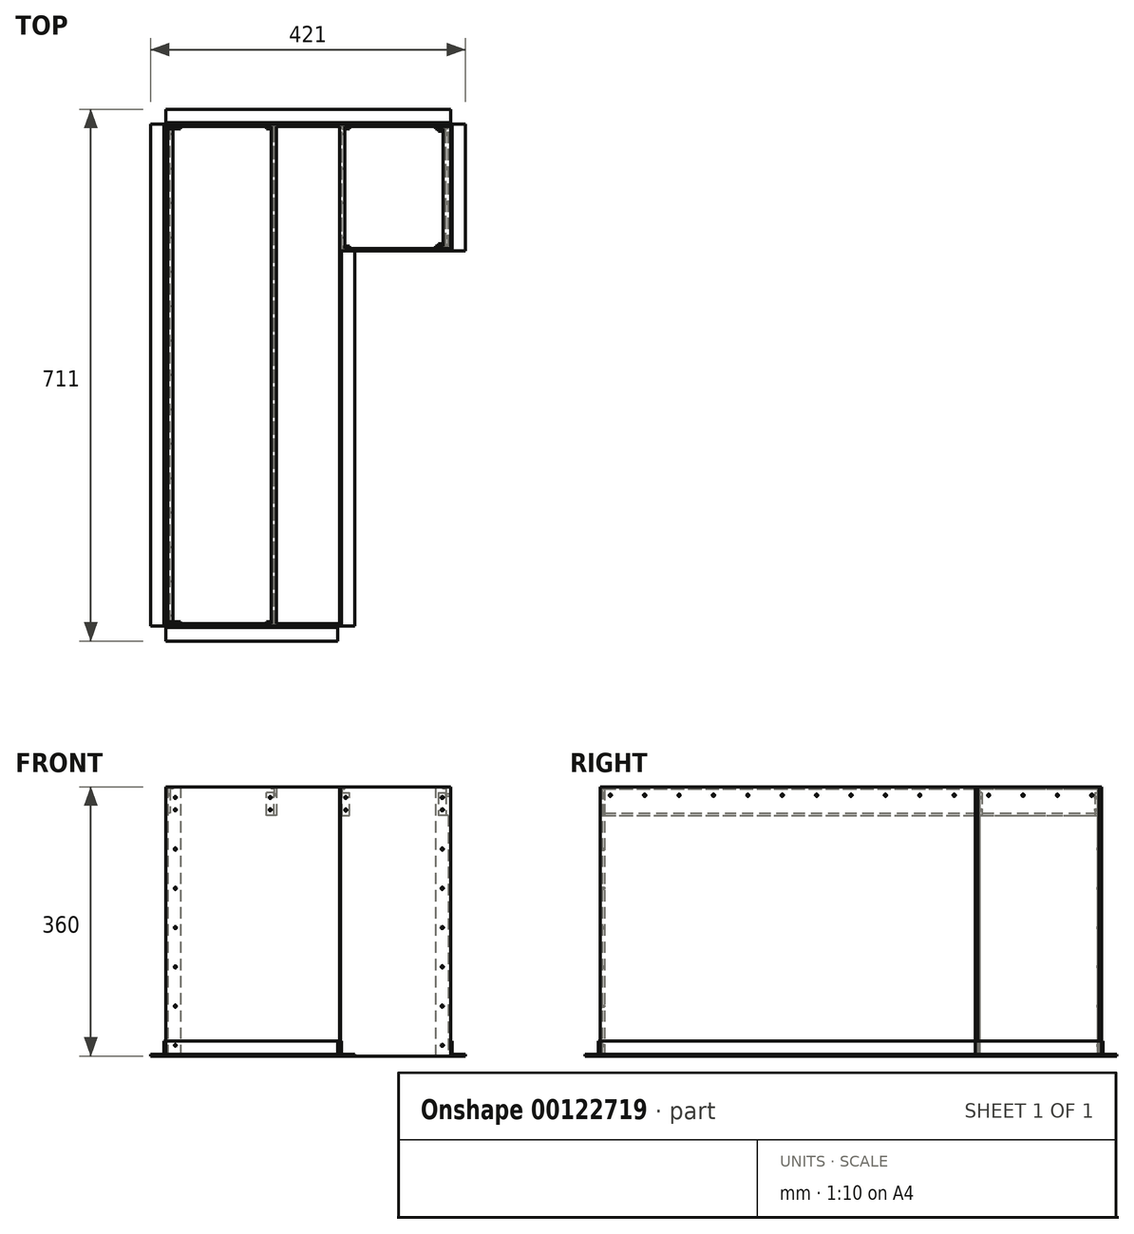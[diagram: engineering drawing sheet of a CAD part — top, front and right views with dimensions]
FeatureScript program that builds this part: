
annotation { "Feature Type Name" : "Feature", "Feature Type Description" : "" }
export const myFeature = defineFeature(function(context is Context, id is Id, definition is map)
    precondition{}
    {
        {
            var Q0;
            Q0=qCreatedBy(makeId("Top.planeOp"),FACE);
            var sketch = newSketch(context, id + "F0", { "sketchPlane" : qUnion([Q0])});
            skLineSegment(sketch, "E0.bottom", {"start": v(0, 0) * mm, "end": v(381, 0) * mm});
            skLineSegment(sketch, "E0.top", {"start": v(0, -3) * mm, "end": v(381, -3) * mm});
            skLineSegment(sketch, "E0.left", {"start": v(0, 0) * mm, "end": v(0, -3) * mm});
            skLineSegment(sketch, "E0.right", {"start": v(381, 0) * mm, "end": v(381, -3) * mm});
            skLineSegment(sketch, "E1.bottom", {"start": v(3, -3) * mm, "end": v(148, -3) * mm, "construction": true});
            skLineSegment(sketch, "E1.top", {"start": v(3, -78) * mm, "end": v(148, -78) * mm, "construction": true});
            skLineSegment(sketch, "E1.left", {"start": v(3, -3) * mm, "end": v(3, -78) * mm, "construction": true});
            skLineSegment(sketch, "E1.right", {"start": v(148, -3) * mm, "end": v(148, -78) * mm, "construction": true});
            skLineSegment(sketch, "E2.bottom", {"start": v(233, -3) * mm, "end": v(378, -3) * mm, "construction": true});
            skLineSegment(sketch, "E2.top", {"start": v(233, -58) * mm, "end": v(378, -58) * mm, "construction": true});
            skLineSegment(sketch, "E2.left", {"start": v(233, -3) * mm, "end": v(233, -58) * mm, "construction": true});
            skLineSegment(sketch, "E2.right", {"start": v(378, -3) * mm, "end": v(378, -58) * mm, "construction": true});
            skSolve(sketch);
        }
        {
            var Q0;
            Q0=qCreatedBy(makeId("Top.planeOp"),FACE);
            var sketch = newSketch(context, id + "F1", { "sketchPlane" : qUnion([Q0])});
            skLineSegment(sketch, "E3.bottom", {"start": v(3, -668) * mm, "end": v(0, -668) * mm});
            skLineSegment(sketch, "E3.top", {"start": v(3, -3) * mm, "end": v(0, -3) * mm});
            skLineSegment(sketch, "E3.left", {"start": v(3, -668) * mm, "end": v(3, -3) * mm});
            skLineSegment(sketch, "E3.right", {"start": v(0, -668) * mm, "end": v(0, -3) * mm});
            skLineSegment(sketch, "E4.bottom", {"start": v(3, -3) * mm, "end": v(20, -3) * mm});
            skLineSegment(sketch, "E4.top", {"start": v(3, -6) * mm, "end": v(20, -6) * mm});
            skLineSegment(sketch, "E4.left", {"start": v(3, -3) * mm, "end": v(3, -6) * mm});
            skLineSegment(sketch, "E4.right", {"start": v(20, -3) * mm, "end": v(20, -6) * mm});
            skLineSegment(sketch, "E5.bottom", {"start": v(3, -668) * mm, "end": v(20, -668) * mm});
            skLineSegment(sketch, "E5.top", {"start": v(3, -665) * mm, "end": v(20, -665) * mm});
            skLineSegment(sketch, "E5.left", {"start": v(3, -668) * mm, "end": v(3, -665) * mm});
            skLineSegment(sketch, "E5.right", {"start": v(20, -668) * mm, "end": v(20, -665) * mm});
            skSolve(sketch);
        }
        {
            var Q0;
            Q0=qCreatedBy(makeId("Top.planeOp"),FACE);
            var sketch = newSketch(context, id + "F2", { "sketchPlane" : qUnion([Q0])});
            skLineSegment(sketch, "E6.bottom", {"start": v(148, -3) * mm, "end": v(233, -3) * mm});
            skLineSegment(sketch, "E6.top", {"start": v(148, -399) * mm, "end": v(233, -399) * mm});
            skLineSegment(sketch, "E6.left", {"start": v(148, -3) * mm, "end": v(148, -399) * mm});
            skLineSegment(sketch, "E6.right", {"start": v(233, -3) * mm, "end": v(233, -399) * mm});
            skLineSegment(sketch, "E7.bottom", {"start": v(161.5, -6) * mm, "end": v(219.5, -6) * mm, "construction": true});
            skLineSegment(sketch, "E7.top", {"start": v(161.5, -67) * mm, "end": v(219.5, -67) * mm, "construction": true});
            skLineSegment(sketch, "E7.left", {"start": v(161.5, -6) * mm, "end": v(161.5, -67) * mm, "construction": true});
            skLineSegment(sketch, "E7.right", {"start": v(219.5, -6) * mm, "end": v(219.5, -67) * mm, "construction": true});
            skLineSegment(sketch, "E8.bottom", {"start": v(148, -400) * mm, "end": v(233, -400) * mm});
            skLineSegment(sketch, "E8.top", {"start": v(148, -668) * mm, "end": v(233, -668) * mm});
            skLineSegment(sketch, "E8.left", {"start": v(148, -400) * mm, "end": v(148, -668) * mm});
            skLineSegment(sketch, "E8.right", {"start": v(233, -400) * mm, "end": v(233, -668) * mm});
            skSolve(sketch);
        }
        {
            var Q0;
            Q0=qCreatedBy(makeId("Top.planeOp"),FACE);
            var sketch = newSketch(context, id + "F3", { "sketchPlane" : qUnion([Q0])});
            skLineSegment(sketch, "E9.bottom", {"start": v(381, -3) * mm, "end": v(378, -3) * mm});
            skLineSegment(sketch, "E9.top", {"start": v(381, -166) * mm, "end": v(378, -166) * mm});
            skLineSegment(sketch, "E9.left", {"start": v(381, -3) * mm, "end": v(381, -166) * mm});
            skLineSegment(sketch, "E9.right", {"start": v(378, -3) * mm, "end": v(378, -166) * mm});
            skLineSegment(sketch, "E10.bottom", {"start": v(378, -3) * mm, "end": v(361, -3) * mm});
            skLineSegment(sketch, "E10.top", {"start": v(378, -6) * mm, "end": v(361, -6) * mm});
            skLineSegment(sketch, "E10.left", {"start": v(378, -3) * mm, "end": v(378, -6) * mm});
            skLineSegment(sketch, "E10.right", {"start": v(361, -3) * mm, "end": v(361, -6) * mm});
            skLineSegment(sketch, "E11.bottom", {"start": v(378, -166) * mm, "end": v(361, -166) * mm});
            skLineSegment(sketch, "E11.top", {"start": v(378, -163) * mm, "end": v(361, -163) * mm});
            skLineSegment(sketch, "E11.left", {"start": v(378, -166) * mm, "end": v(378, -163) * mm});
            skLineSegment(sketch, "E11.right", {"start": v(361, -166) * mm, "end": v(361, -163) * mm});
            skSolve(sketch);
        }
        {
            var Q0;
            Q0=qCreatedBy(makeId("Top.planeOp"),FACE);
            var sketch = newSketch(context, id + "F4", { "sketchPlane" : qUnion([Q0])});
            skLineSegment(sketch, "E12.bottom", {"start": v(0, -668) * mm, "end": v(233, -668) * mm});
            skLineSegment(sketch, "E12.top", {"start": v(0, -671) * mm, "end": v(233, -671) * mm});
            skLineSegment(sketch, "E12.left", {"start": v(0, -668) * mm, "end": v(0, -671) * mm});
            skLineSegment(sketch, "E12.right", {"start": v(233, -668) * mm, "end": v(233, -671) * mm});
            skSolve(sketch);
        }
        {
            var Q0;
            Q0=qCreatedBy(makeId("Top.planeOp"),FACE);
            var sketch = newSketch(context, id + "F5", { "sketchPlane" : qUnion([Q0])});
            skLineSegment(sketch, "E13.bottom", {"start": v(233, -166) * mm, "end": v(381, -166) * mm});
            skLineSegment(sketch, "E13.top", {"start": v(233, -169) * mm, "end": v(381, -169) * mm});
            skLineSegment(sketch, "E13.left", {"start": v(233, -166) * mm, "end": v(233, -169) * mm});
            skLineSegment(sketch, "E13.right", {"start": v(381, -166) * mm, "end": v(381, -169) * mm});
            skSolve(sketch);
        }
        {
            var Q0;
            Q0=qCreatedBy(makeId("Top.planeOp"),FACE);
            var sketch = newSketch(context, id + "F6", { "sketchPlane" : qUnion([Q0])});
            skLineSegment(sketch, "E14.bottom", {"start": v(145, -3) * mm, "end": v(125, -3) * mm});
            skLineSegment(sketch, "E14.top", {"start": v(145, -6) * mm, "end": v(125, -6) * mm});
            skLineSegment(sketch, "E14.left", {"start": v(145, -3) * mm, "end": v(145, -6) * mm});
            skLineSegment(sketch, "E14.right", {"start": v(125, -3) * mm, "end": v(125, -6) * mm});
            skLineSegment(sketch, "E15.bottom", {"start": v(145, -6) * mm, "end": v(142, -6) * mm});
            skLineSegment(sketch, "E15.top", {"start": v(145, -668) * mm, "end": v(142, -668) * mm});
            skLineSegment(sketch, "E15.left", {"start": v(145, -6) * mm, "end": v(145, -668) * mm});
            skLineSegment(sketch, "E15.right", {"start": v(142, -6) * mm, "end": v(142, -668) * mm});
            skLineSegment(sketch, "E16.bottom", {"start": v(142, -668) * mm, "end": v(125, -668) * mm});
            skLineSegment(sketch, "E16.top", {"start": v(142, -665) * mm, "end": v(125, -665) * mm});
            skLineSegment(sketch, "E16.left", {"start": v(142, -668) * mm, "end": v(142, -665) * mm});
            skLineSegment(sketch, "E16.right", {"start": v(125, -668) * mm, "end": v(125, -665) * mm});
            skSolve(sketch);
        }
        {
            var Q0;
            Q0=makeQuery(id+"F0.imprint","IMPRINT",FACE,{"disambiguationData":[TD([[makeQuery(id+"F0.imprint","IMPRINT",EDGE,{"derivedFrom":sQuery(id+"F0.wireOp",EDGE,"E0.bottom")}),-1.0]])]});
            var Q1;
            Q1=makeQuery(id+"F1.imprint","IMPRINT",FACE,{"disambiguationData":[TD([[makeQuery(id+"F1.imprint","IMPRINT",EDGE,{"derivedFrom":sQuery(id+"F1.wireOp",EDGE,"E4.bottom")}),-1.0]])]});
            var Q2;
            Q2=makeQuery(id+"F1.imprint","IMPRINT",FACE,{"disambiguationData":[TD([[makeQuery(id+"F1.imprint","IMPRINT",EDGE,{"derivedFrom":sQuery(id+"F1.wireOp",EDGE,"E5.bottom")}),1.0]])]});
            var Q3;
            Q3=makeQuery(id+"F1.imprint","IMPRINT",FACE,{"disambiguationData":[TD([[makeQuery(id+"F1.imprint","IMPRINT",EDGE,{"derivedFrom":sQuery(id+"F1.wireOp",EDGE,"E3.bottom")}),-1.0]])]});
            var Q4;
            Q4=makeQuery(id+"F3.imprint","IMPRINT",FACE,{"disambiguationData":[TD([[makeQuery(id+"F3.imprint","IMPRINT",EDGE,{"derivedFrom":sQuery(id+"F3.wireOp",EDGE,"E10.bottom")}),1.0]])]});
            var Q5;
            Q5=makeQuery(id+"F3.imprint","IMPRINT",FACE,{"disambiguationData":[TD([[makeQuery(id+"F3.imprint","IMPRINT",EDGE,{"derivedFrom":sQuery(id+"F3.wireOp",EDGE,"E11.bottom")}),-1.0]])]});
            var Q6;
            Q6=makeQuery(id+"F3.imprint","IMPRINT",FACE,{"disambiguationData":[TD([[makeQuery(id+"F3.imprint","IMPRINT",EDGE,{"derivedFrom":sQuery(id+"F3.wireOp",EDGE,"E9.bottom")}),1.0]])]});
            var Q7;
            Q7=makeQuery(id+"F4.imprint","IMPRINT",FACE,{"disambiguationData":[TD([[makeQuery(id+"F4.imprint","IMPRINT",EDGE,{"derivedFrom":sQuery(id+"F4.wireOp",EDGE,"E12.bottom")}),-1.0]])]});
            var Q8;
            Q8=makeQuery(id+"F5.imprint","IMPRINT",FACE,{"disambiguationData":[TD([[makeQuery(id+"F5.imprint","IMPRINT",EDGE,{"derivedFrom":sQuery(id+"F5.wireOp",EDGE,"E13.bottom")}),-1.0]])]});
            extrude(context, id + "F7", {"entities" : qUnion([Q0, Q1, Q2, Q3, Q4, Q5, Q6, Q7, Q8]), "depth" : 360 * mm});
        }
        {
            var Q0;
            Q0=makeQuery(id+"F7.opExtrude","SWEPT_FACE",FACE,{"disambiguationData":[OSD([sQuery(id+"F0.wireOp",EDGE,"E0.bottom")])]});
            var sketch = newSketch(context, id + "F8", { "sketchPlane" : qUnion([Q0])});
            skLineSegment(sketch, "E17.bottom", {"start": v(0, 0) * mm, "end": v(2, 0) * mm});
            skLineSegment(sketch, "E17.top", {"start": v(0, 20) * mm, "end": v(2, 20) * mm});
            skLineSegment(sketch, "E17.left", {"start": v(0, 0) * mm, "end": v(0, 20) * mm});
            skLineSegment(sketch, "E17.right", {"start": v(2, 0) * mm, "end": v(2, 20) * mm});
            skLineSegment(sketch, "E18.bottom", {"start": v(2, 0) * mm, "end": v(20, 0) * mm});
            skLineSegment(sketch, "E18.top", {"start": v(2, 2) * mm, "end": v(20, 2) * mm});
            skLineSegment(sketch, "E18.left", {"start": v(2, 0) * mm, "end": v(2, 2) * mm});
            skLineSegment(sketch, "E18.right", {"start": v(20, 0) * mm, "end": v(20, 2) * mm});
            skSolve(sketch);
        }
        {
            var Q0;
            Q0 = qSketchRegion(id + "F8", true);
            extrude(context, id + "F9", {"entities" : qUnion([Q0]), "oppositeDirection" : true, "depth" : 671 * mm});
        }
        {
            var Q0;
            Q0=makeQuery(id+"F7.opExtrude","SWEPT_FACE",FACE,{"disambiguationData":[OSD([sQuery(id+"F1.wireOp",EDGE,"E3.right")])]});
            var sketch = newSketch(context, id + "F10", { "sketchPlane" : qUnion([Q0])});
            skLineSegment(sketch, "E19.bottom", {"start": v(671, 20) * mm, "end": v(673, 20) * mm});
            skLineSegment(sketch, "E19.top", {"start": v(671, 0) * mm, "end": v(673, 0) * mm});
            skLineSegment(sketch, "E19.left", {"start": v(671, 20) * mm, "end": v(671, 0) * mm});
            skLineSegment(sketch, "E19.right", {"start": v(673, 20) * mm, "end": v(673, 0) * mm});
            skLineSegment(sketch, "E20.bottom", {"start": v(673, 0) * mm, "end": v(691, 0) * mm});
            skLineSegment(sketch, "E20.top", {"start": v(673, 2) * mm, "end": v(691, 2) * mm});
            skLineSegment(sketch, "E20.left", {"start": v(673, 0) * mm, "end": v(673, 2) * mm});
            skLineSegment(sketch, "E20.right", {"start": v(691, 0) * mm, "end": v(691, 2) * mm});
            skSolve(sketch);
        }
        {
            var Q0;
            Q0 = qSketchRegion(id + "F10", true);
            extrude(context, id + "F11", {"entities" : qUnion([Q0]), "operationType" : NewBodyOperationType.ADD, "oppositeDirection" : true, "depth" : 230 * mm});
        }
        {
            var Q0;
            Q0=makeQuery(id+"F7.opExtrude","SWEPT_FACE",FACE,{"disambiguationData":[OSD([sQuery(id+"F4.wireOp",EDGE,"E12.top")])]});
            var sketch = newSketch(context, id + "F12", { "sketchPlane" : qUnion([Q0])});
            skLineSegment(sketch, "E21.bottom", {"start": v(233, 0) * mm, "end": v(235, 0) * mm});
            skLineSegment(sketch, "E21.top", {"start": v(233, 20) * mm, "end": v(235, 20) * mm});
            skLineSegment(sketch, "E21.left", {"start": v(233, 0) * mm, "end": v(233, 20) * mm});
            skLineSegment(sketch, "E21.right", {"start": v(235, 0) * mm, "end": v(235, 20) * mm});
            skLineSegment(sketch, "E22.bottom", {"start": v(235, 0) * mm, "end": v(253, 0) * mm});
            skLineSegment(sketch, "E22.top", {"start": v(235, 2) * mm, "end": v(253, 2) * mm});
            skLineSegment(sketch, "E22.left", {"start": v(235, 0) * mm, "end": v(235, 2) * mm});
            skLineSegment(sketch, "E22.right", {"start": v(253, 0) * mm, "end": v(253, 2) * mm});
            skSolve(sketch);
        }
        {
            var Q0;
            Q0 = qSketchRegion(id + "F12", true);
            extrude(context, id + "F13", {"entities" : qUnion([Q0]), "oppositeDirection" : true, "depth" : 502 * mm});
        }
        {
            var Q0;
            Q0=makeQuery(id+"F7.opExtrude","SWEPT_FACE",FACE,{"disambiguationData":[OSD([sQuery(id+"F5.wireOp",EDGE,"E13.top")])]});
            var sketch = newSketch(context, id + "F14", { "sketchPlane" : qUnion([Q0])});
            skLineSegment(sketch, "E23.bottom", {"start": v(381, 0) * mm, "end": v(383, 0) * mm});
            skLineSegment(sketch, "E23.top", {"start": v(381, 20) * mm, "end": v(383, 20) * mm});
            skLineSegment(sketch, "E23.left", {"start": v(381, 0) * mm, "end": v(381, 20) * mm});
            skLineSegment(sketch, "E23.right", {"start": v(383, 0) * mm, "end": v(383, 20) * mm});
            skLineSegment(sketch, "E24.bottom", {"start": v(383, 0) * mm, "end": v(401, 0) * mm});
            skLineSegment(sketch, "E24.top", {"start": v(383, 2) * mm, "end": v(401, 2) * mm});
            skLineSegment(sketch, "E24.left", {"start": v(383, 0) * mm, "end": v(383, 2) * mm});
            skLineSegment(sketch, "E24.right", {"start": v(401, 0) * mm, "end": v(401, 2) * mm});
            skSolve(sketch);
        }
        {
            var Q0;
            Q0 = qSketchRegion(id + "F14", true);
            extrude(context, id + "F15", {"entities" : qUnion([Q0]), "oppositeDirection" : true, "depth" : 169 * mm});
        }
        {
            var Q0;
            Q0=makeQuery(id+"F7.opExtrude","SWEPT_FACE",FACE,{"disambiguationData":[OSD([sQuery(id+"F0.wireOp",EDGE,"E0.right")])]});
            var sketch = newSketch(context, id + "F16", { "sketchPlane" : qUnion([Q0])});
            skLineSegment(sketch, "E25.bottom", {"start": v(0, 0) * mm, "end": v(2, 0) * mm});
            skLineSegment(sketch, "E25.top", {"start": v(0, 20) * mm, "end": v(2, 20) * mm});
            skLineSegment(sketch, "E25.left", {"start": v(0, 0) * mm, "end": v(0, 20) * mm});
            skLineSegment(sketch, "E25.right", {"start": v(2, 0) * mm, "end": v(2, 20) * mm});
            skLineSegment(sketch, "E26.bottom", {"start": v(2, 0) * mm, "end": v(20, 0) * mm});
            skLineSegment(sketch, "E26.top", {"start": v(2, 2) * mm, "end": v(20, 2) * mm});
            skLineSegment(sketch, "E26.left", {"start": v(2, 0) * mm, "end": v(2, 2) * mm});
            skLineSegment(sketch, "E26.right", {"start": v(20, 0) * mm, "end": v(20, 2) * mm});
            skSolve(sketch);
        }
        {
            var Q0;
            Q0 = qSketchRegion(id + "F16", true);
            extrude(context, id + "F17", {"entities" : qUnion([Q0]), "oppositeDirection" : true, "depth" : 381 * mm});
        }
        {
            var Q0;
            Q0=makeQuery(id+"F7.opExtrude","CAP_FACE",FACE,{"disambiguationData":[OSD([sQuery(id+"F4.wireOp",EDGE,"E12.bottom"),sQuery(id+"F4.wireOp",EDGE,"E12.top"),sQuery(id+"F4.wireOp",EDGE,"E12.left"),sQuery(id+"F4.wireOp",EDGE,"E12.right")])],"isStart":false});
            var sketch = newSketch(context, id + "F18", { "sketchPlane" : qUnion([Q0])});
            skLineSegment(sketch, "E27.bottom", {"start": v(233, -169) * mm, "end": v(234, -169) * mm});
            skLineSegment(sketch, "E27.top", {"start": v(233, -671) * mm, "end": v(234, -671) * mm});
            skLineSegment(sketch, "E27.left", {"start": v(233, -169) * mm, "end": v(233, -671) * mm});
            skLineSegment(sketch, "E27.right", {"start": v(234, -169) * mm, "end": v(234, -671) * mm});
            skSolve(sketch);
        }
        {
            var Q0;
            Q0 = qSketchRegion(id + "F18", true);
            extrude(context, id + "F19", {"entities" : qUnion([Q0]), "oppositeDirection" : true, "depth" : 360 * mm});
        }
        {
            var Q0;
            Q0=makeQuery(id+"F7.opExtrude","SWEPT_FACE",FACE,{"disambiguationData":[OSD([sQuery(id+"F1.wireOp",EDGE,"E4.top")])]});
            var sketch = newSketch(context, id + "F20", { "sketchPlane" : qUnion([Q0])});
            skLineSegment(sketch, "E28.bottom", {"start": v(10, 360) * mm, "end": v(6, 360) * mm});
            skLineSegment(sketch, "E28.top", {"start": v(10, 357) * mm, "end": v(6, 357) * mm});
            skLineSegment(sketch, "E28.left", {"start": v(10, 360) * mm, "end": v(10, 357) * mm});
            skLineSegment(sketch, "E28.right", {"start": v(6, 360) * mm, "end": v(6, 357) * mm});
            skLineSegment(sketch, "E29.bottom", {"start": v(6, 360) * mm, "end": v(3, 360) * mm});
            skLineSegment(sketch, "E29.top", {"start": v(6, 325) * mm, "end": v(3, 325) * mm});
            skLineSegment(sketch, "E29.left", {"start": v(6, 360) * mm, "end": v(6, 325) * mm});
            skLineSegment(sketch, "E29.right", {"start": v(3, 360) * mm, "end": v(3, 325) * mm});
            skSolve(sketch);
        }
        {
            var Q0;
            Q0 = qSketchRegion(id + "F20", true);
            extrude(context, id + "F21", {"entities" : qUnion([Q0]), "depth" : 659 * mm});
        }
        {
            var Q0;
            Q0=makeQuery(id+"F7.opExtrude","SWEPT_FACE",FACE,{"disambiguationData":[OSD([sQuery(id+"F0.wireOp",EDGE,"E0.top")])]});
            var sketch = newSketch(context, id + "F22", { "sketchPlane" : qUnion([Q0])});
            skLineSegment(sketch, "E30.bottom", {"start": v(148, 360) * mm, "end": v(141, 360) * mm});
            skLineSegment(sketch, "E30.top", {"start": v(148, 357) * mm, "end": v(141, 357) * mm});
            skLineSegment(sketch, "E30.left", {"start": v(148, 360) * mm, "end": v(148, 357) * mm});
            skLineSegment(sketch, "E30.right", {"start": v(141, 360) * mm, "end": v(141, 357) * mm});
            skLineSegment(sketch, "E31.bottom", {"start": v(148, 357) * mm, "end": v(145, 357) * mm});
            skLineSegment(sketch, "E31.top", {"start": v(148, 322) * mm, "end": v(145, 322) * mm});
            skLineSegment(sketch, "E31.left", {"start": v(148, 357) * mm, "end": v(148, 322) * mm});
            skLineSegment(sketch, "E31.right", {"start": v(145, 357) * mm, "end": v(145, 322) * mm});
            skSolve(sketch);
        }
        {
            var Q0;
            Q0 = qSketchRegion(id + "F22", true);
            extrude(context, id + "F23", {"entities" : qUnion([Q0]), "depth" : 665 * mm});
        }
        {
            var Q0;
            Q0=makeQuery(id+"F7.opExtrude","SWEPT_FACE",FACE,{"disambiguationData":[OSD([sQuery(id+"F0.wireOp",EDGE,"E0.top")])]});
            var sketch = newSketch(context, id + "F24", { "sketchPlane" : qUnion([Q0])});
            skLineSegment(sketch, "E32.bottom", {"start": v(145, 322) * mm, "end": v(135, 322) * mm});
            skLineSegment(sketch, "E32.top", {"start": v(145, 352) * mm, "end": v(135, 352) * mm});
            skLineSegment(sketch, "E32.left", {"start": v(145, 322) * mm, "end": v(145, 352) * mm});
            skLineSegment(sketch, "E32.right", {"start": v(135, 322) * mm, "end": v(135, 352) * mm});
            skSolve(sketch);
        }
        {
            var Q0;
            Q0 = qSketchRegion(id + "F24", true);
            extrude(context, id + "F25", {"entities" : qUnion([Q0]), "operationType" : NewBodyOperationType.ADD, "depth" : 3 * mm});
        }
        {
            var Q0;
            Q0=makeQuery(id+"F7.opExtrude","SWEPT_FACE",FACE,{"disambiguationData":[OSD([sQuery(id+"F4.wireOp",EDGE,"E12.bottom")])]});
            var sketch = newSketch(context, id + "F26", { "sketchPlane" : qUnion([Q0])});
            skLineSegment(sketch, "E33.bottom", {"start": v(-145, 322) * mm, "end": v(-135, 322) * mm});
            skLineSegment(sketch, "E33.top", {"start": v(-145, 352) * mm, "end": v(-135, 352) * mm});
            skLineSegment(sketch, "E33.left", {"start": v(-145, 322) * mm, "end": v(-145, 352) * mm});
            skLineSegment(sketch, "E33.right", {"start": v(-135, 322) * mm, "end": v(-135, 352) * mm});
            skSolve(sketch);
        }
        {
            var Q0;
            Q0 = qSketchRegion(id + "F26", true);
            extrude(context, id + "F27", {"entities" : qUnion([Q0]), "operationType" : NewBodyOperationType.ADD, "depth" : 3 * mm});
        }
        {
            var Q0;
            Q0=makeQuery(id+"F7.opExtrude","SWEPT_FACE",FACE,{"disambiguationData":[OSD([sQuery(id+"F3.wireOp",EDGE,"E10.top")])]});
            var sketch = newSketch(context, id + "F28", { "sketchPlane" : qUnion([Q0])});
            skLineSegment(sketch, "E34.bottom", {"start": v(378, 357) * mm, "end": v(375, 357) * mm});
            skLineSegment(sketch, "E34.top", {"start": v(378, 322) * mm, "end": v(375, 322) * mm});
            skLineSegment(sketch, "E34.left", {"start": v(378, 357) * mm, "end": v(378, 322) * mm});
            skLineSegment(sketch, "E34.right", {"start": v(375, 357) * mm, "end": v(375, 322) * mm});
            skLineSegment(sketch, "E35.bottom", {"start": v(378, 357) * mm, "end": v(371, 357) * mm});
            skLineSegment(sketch, "E35.top", {"start": v(378, 360) * mm, "end": v(371, 360) * mm});
            skLineSegment(sketch, "E35.left", {"start": v(378, 357) * mm, "end": v(378, 360) * mm});
            skLineSegment(sketch, "E35.right", {"start": v(371, 357) * mm, "end": v(371, 360) * mm});
            skSolve(sketch);
        }
        {
            var Q0;
            Q0 = qSketchRegion(id + "F28", true);
            extrude(context, id + "F29", {"entities" : qUnion([Q0]), "depth" : 157 * mm});
        }
        {
            var Q0;
            Q0=makeQuery(id+"F7.opExtrude","SWEPT_FACE",FACE,{"disambiguationData":[OSD([sQuery(id+"F3.wireOp",EDGE,"E10.top")])]});
            var sketch = newSketch(context, id + "F30", { "sketchPlane" : qUnion([Q0])});
            skLineSegment(sketch, "E36.bottom", {"start": v(365, 352) * mm, "end": v(375, 352) * mm});
            skLineSegment(sketch, "E36.top", {"start": v(365, 322) * mm, "end": v(375, 322) * mm});
            skLineSegment(sketch, "E36.left", {"start": v(365, 352) * mm, "end": v(365, 322) * mm});
            skLineSegment(sketch, "E36.right", {"start": v(375, 352) * mm, "end": v(375, 322) * mm});
            skSolve(sketch);
        }
        {
            var Q0;
            Q0 = qSketchRegion(id + "F30", true);
            extrude(context, id + "F31", {"entities" : qUnion([Q0]), "operationType" : NewBodyOperationType.ADD, "depth" : 3 * mm});
        }
        {
            var Q0;
            Q0=makeQuery(id+"F7.opExtrude","SWEPT_FACE",FACE,{"disambiguationData":[OSD([sQuery(id+"F3.wireOp",EDGE,"E11.top")])]});
            var sketch = newSketch(context, id + "F32", { "sketchPlane" : qUnion([Q0])});
            skLineSegment(sketch, "E37.bottom", {"start": v(-375, 352) * mm, "end": v(-365, 352) * mm});
            skLineSegment(sketch, "E37.top", {"start": v(-375, 322) * mm, "end": v(-365, 322) * mm});
            skLineSegment(sketch, "E37.left", {"start": v(-375, 352) * mm, "end": v(-375, 322) * mm});
            skLineSegment(sketch, "E37.right", {"start": v(-365, 352) * mm, "end": v(-365, 322) * mm});
            skSolve(sketch);
        }
        {
            var Q0;
            Q0 = qSketchRegion(id + "F32", true);
            extrude(context, id + "F33", {"entities" : qUnion([Q0]), "operationType" : NewBodyOperationType.ADD, "depth" : 3 * mm});
        }
        {
            var Q0;
            Q0=makeQuery(id+"F7.opExtrude","SWEPT_FACE",FACE,{"disambiguationData":[OSD([sQuery(id+"F0.wireOp",EDGE,"E0.top")])]});
            var sketch = newSketch(context, id + "F34", { "sketchPlane" : qUnion([Q0])});
            skLineSegment(sketch, "E38.bottom", {"start": v(233, 357) * mm, "end": v(236, 357) * mm});
            skLineSegment(sketch, "E38.top", {"start": v(233, 322) * mm, "end": v(236, 322) * mm});
            skLineSegment(sketch, "E38.left", {"start": v(233, 357) * mm, "end": v(233, 322) * mm});
            skLineSegment(sketch, "E38.right", {"start": v(236, 357) * mm, "end": v(236, 322) * mm});
            skLineSegment(sketch, "E39.bottom", {"start": v(233, 357) * mm, "end": v(240, 357) * mm});
            skLineSegment(sketch, "E39.top", {"start": v(233, 360) * mm, "end": v(240, 360) * mm});
            skLineSegment(sketch, "E39.left", {"start": v(233, 357) * mm, "end": v(233, 360) * mm});
            skLineSegment(sketch, "E39.right", {"start": v(240, 357) * mm, "end": v(240, 360) * mm});
            skSolve(sketch);
        }
        {
            var Q0;
            Q0 = qSketchRegion(id + "F34", true);
            extrude(context, id + "F35", {"entities" : qUnion([Q0]), "depth" : 163 * mm});
        }
        {
            var Q0;
            Q0=makeQuery(id+"F34.imprint","IMPRINT",FACE,{"disambiguationData":[TD([[makeQuery(id+"F34.imprint","IMPRINT",EDGE,{"derivedFrom":sQuery(id+"F34.wireOp",EDGE,"E38.top")}),-1.0]])]});
            var sketch = newSketch(context, id + "F36", { "sketchPlane" : qUnion([Q0])});
            skLineSegment(sketch, "E40.bottom", {"start": v(236, 322) * mm, "end": v(246, 322) * mm});
            skLineSegment(sketch, "E40.top", {"start": v(236, 352) * mm, "end": v(246, 352) * mm});
            skLineSegment(sketch, "E40.left", {"start": v(236, 322) * mm, "end": v(236, 352) * mm});
            skLineSegment(sketch, "E40.right", {"start": v(246, 322) * mm, "end": v(246, 352) * mm});
            skSolve(sketch);
        }
        {
            var Q0;
            Q0=makeQuery(id+"F36.imprint","IMPRINT",FACE,{"disambiguationData":[TD([[makeQuery(id+"F36.imprint","IMPRINT",EDGE,{"derivedFrom":sQuery(id+"F36.wireOp",EDGE,"E40.bottom")}),1.0]])]});
            extrude(context, id + "F37", {"entities" : qUnion([Q0]), "operationType" : NewBodyOperationType.ADD, "depth" : 3 * mm});
        }
        {
            var Q0;
            Q0=makeQuery(id+"F7.opExtrude","SWEPT_FACE",FACE,{"disambiguationData":[OSD([sQuery(id+"F5.wireOp",EDGE,"E13.bottom")])]});
            var sketch = newSketch(context, id + "F38", { "sketchPlane" : qUnion([Q0])});
            skLineSegment(sketch, "E41.bottom", {"start": v(-236, 322) * mm, "end": v(-246, 322) * mm});
            skLineSegment(sketch, "E41.top", {"start": v(-236, 352) * mm, "end": v(-246, 352) * mm});
            skLineSegment(sketch, "E41.left", {"start": v(-236, 322) * mm, "end": v(-236, 352) * mm});
            skLineSegment(sketch, "E41.right", {"start": v(-246, 322) * mm, "end": v(-246, 352) * mm});
            skSolve(sketch);
        }
        {
            var Q0;
            Q0 = qSketchRegion(id + "F38", true);
            extrude(context, id + "F39", {"entities" : qUnion([Q0]), "operationType" : NewBodyOperationType.ADD, "depth" : 3 * mm});
        }
        {
            var Q0;
            {var subQ0=sQuery(id+"F1.wireOp",EDGE,"E3.right");Q0=makeQuery(id+"F10.imprint","IMPRINT",FACE,{"disambiguationData":[TD([[makeQuery(id+"F10.imprint","IMPRINT",EDGE,{"derivedFrom":makeQuery(id+"F7.opExtrude","CAP_EDGE",EDGE,{"disambiguationData":[OSD([subQ0])],"isStart":true})}),-1.0]])]});}
            var sketch = newSketch(context, id + "F40", { "sketchPlane" : qUnion([Q0])});
            skCircle(sketch, "E42", {"center": v(13.25, 348.75) * mm, "radius": 1.25 * mm});
            skCircle(sketch, "E43", {"center": v(59.25, 348.75) * mm, "radius": 1.25 * mm});
            skCircle(sketch, "E44", {"center": v(105.25, 348.75) * mm, "radius": 1.25 * mm});
            skCircle(sketch, "E45", {"center": v(151.25, 348.75) * mm, "radius": 1.25 * mm});
            skCircle(sketch, "E46", {"center": v(197.25, 348.75) * mm, "radius": 1.25 * mm});
            skCircle(sketch, "E47", {"center": v(243.25, 348.75) * mm, "radius": 1.25 * mm});
            skCircle(sketch, "E48", {"center": v(289.25, 348.75) * mm, "radius": 1.25 * mm});
            skCircle(sketch, "E49", {"center": v(335.25, 348.75) * mm, "radius": 1.25 * mm});
            skCircle(sketch, "E50", {"center": v(381.25, 348.75) * mm, "radius": 1.25 * mm});
            skCircle(sketch, "E51", {"center": v(427.25, 348.75) * mm, "radius": 1.25 * mm});
            skCircle(sketch, "E52", {"center": v(473.25, 348.75) * mm, "radius": 1.25 * mm});
            skCircle(sketch, "E53", {"center": v(519.25, 348.75) * mm, "radius": 1.25 * mm});
            skCircle(sketch, "E54", {"center": v(565.25, 348.75) * mm, "radius": 1.25 * mm});
            skCircle(sketch, "E55", {"center": v(611.25, 348.75) * mm, "radius": 1.25 * mm});
            skCircle(sketch, "E56", {"center": v(657.25, 348.75) * mm, "radius": 1.25 * mm});
            skSolve(sketch);
        }
        {
            var Q0;
            {var subQ3=sQuery(id+"F8.wireOp",EDGE,"E17.left");Q0=makeQuery(id+"F8.imprint","IMPRINT",FACE,{"disambiguationData":[TD([[makeQuery(id+"F8.imprint","IMPRINT",EDGE,{"derivedFrom":subQ3}),-1.0]])]});}
            var sketch = newSketch(context, id + "F41", { "sketchPlane" : qUnion([Q0])});
            skCircle(sketch, "E57", {"center": v(-370, 345.75) * mm, "radius": 1.25 * mm});
            skCircle(sketch, "E58", {"center": v(-370, 329.25) * mm, "radius": 1.25 * mm});
            skCircle(sketch, "E59", {"center": v(-370, 276.75) * mm, "radius": 1.25 * mm});
            skCircle(sketch, "E60", {"center": v(-370, 224.25) * mm, "radius": 1.25 * mm});
            skCircle(sketch, "E61", {"center": v(-370, 171.75) * mm, "radius": 1.25 * mm});
            skCircle(sketch, "E62", {"center": v(-370, 119.25) * mm, "radius": 1.25 * mm});
            skCircle(sketch, "E63", {"center": v(-370, 66.75) * mm, "radius": 1.25 * mm});
            skCircle(sketch, "E64", {"center": v(-370, 14.25) * mm, "radius": 1.25 * mm});
            skCircle(sketch, "E65", {"center": v(-13, 345.75) * mm, "radius": 1.25 * mm});
            skCircle(sketch, "E66", {"center": v(-13, 329.25) * mm, "radius": 1.25 * mm});
            skCircle(sketch, "E67", {"center": v(-13, 276.75) * mm, "radius": 1.25 * mm});
            skCircle(sketch, "E68", {"center": v(-13, 224.25) * mm, "radius": 1.25 * mm});
            skCircle(sketch, "E69", {"center": v(-13, 171.75) * mm, "radius": 1.25 * mm});
            skCircle(sketch, "E70", {"center": v(-13, 119.25) * mm, "radius": 1.25 * mm});
            skCircle(sketch, "E71", {"center": v(-13, 66.75) * mm, "radius": 1.25 * mm});
            skCircle(sketch, "E72", {"center": v(-13, 14.25) * mm, "radius": 1.25 * mm});
            skCircle(sketch, "E73", {"center": v(-140, 345.75) * mm, "radius": 1.25 * mm});
            skCircle(sketch, "E74", {"center": v(-140, 329.25) * mm, "radius": 1.25 * mm});
            skCircle(sketch, "E75", {"center": v(-241, 345.75) * mm, "radius": 1.25 * mm});
            skCircle(sketch, "E76", {"center": v(-241, 329) * mm, "radius": 1.25 * mm});
            skSolve(sketch);
        }
        {
            var Q0;
            Q0 = qSketchRegion(id + "F41", true);
            extrude(context, id + "F42", {"entities" : qUnion([Q0]), "operationType" : NewBodyOperationType.REMOVE, "endBound" : BoundingType.THROUGH_ALL, "oppositeDirection" : true, "depth" : 25 * mm});
        }
        {
            var Q0;
            Q0=sQuery(id+"F41.wireOp",VERTEX,"E57.center");
            var Q1;
            Q1=sQuery(id+"F41.wireOp",VERTEX,"E58.center");
            var Q2;
            Q2=sQuery(id+"F41.wireOp",VERTEX,"E59.center");
            var Q3;
            Q3=sQuery(id+"F41.wireOp",VERTEX,"E60.center");
            var Q4;
            Q4=sQuery(id+"F41.wireOp",VERTEX,"E61.center");
            var Q5;
            Q5=sQuery(id+"F41.wireOp",VERTEX,"E62.center");
            var Q6;
            Q6=sQuery(id+"F41.wireOp",VERTEX,"E63.center");
            var Q7;
            Q7=sQuery(id+"F41.wireOp",VERTEX,"E64.center");
            var Q8;
            Q8=sQuery(id+"F41.wireOp",VERTEX,"E75.center");
            var Q9;
            Q9=sQuery(id+"F41.wireOp",VERTEX,"E76.center");
            var Q10;
            Q10=sQuery(id+"F41.wireOp",VERTEX,"E73.center");
            var Q11;
            Q11=sQuery(id+"F41.wireOp",VERTEX,"E74.center");
            var Q12;
            Q12=sQuery(id+"F41.wireOp",VERTEX,"E65.center");
            var Q13;
            Q13=sQuery(id+"F41.wireOp",VERTEX,"E66.center");
            var Q14;
            Q14=sQuery(id+"F41.wireOp",VERTEX,"E67.center");
            var Q15;
            Q15=sQuery(id+"F41.wireOp",VERTEX,"E68.center");
            var Q16;
            Q16=sQuery(id+"F41.wireOp",VERTEX,"E69.center");
            var Q17;
            Q17=sQuery(id+"F41.wireOp",VERTEX,"E70.center");
            var Q18;
            Q18=sQuery(id+"F41.wireOp",VERTEX,"E71.center");
            var Q19;
            Q19=sQuery(id+"F44.wireOp",VERTEX,"E84.center");
            var Q20;
            Q20=makeQuery(id+"F7.opExtrude","SWEPT_BODY",BODY,{"disambiguationData":[OSD([sQuery(id+"F0.wireOp",EDGE,"E0.bottom"),sQuery(id+"F0.wireOp",EDGE,"E0.top"),sQuery(id+"F0.wireOp",EDGE,"E0.left"),sQuery(id+"F0.wireOp",EDGE,"E0.right")])]});
            var Q21;
            Q21=makeQuery(id+"F17.opExtrude","SWEPT_BODY",BODY,{"disambiguationData":[OSD([sQuery(id+"F16.wireOp",EDGE,"E25.bottom"),sQuery(id+"F16.wireOp",EDGE,"E25.top"),sQuery(id+"F16.wireOp",EDGE,"E25.left"),sQuery(id+"F16.wireOp",EDGE,"E25.right"),sQuery(id+"F16.wireOp",EDGE,"E26.bottom"),sQuery(id+"F16.wireOp",EDGE,"E26.top"),sQuery(id+"F16.wireOp",EDGE,"E26.right")])]});
            var Q22;
            Q22=makeQuery(id+"F7.opExtrude","SWEPT_BODY",BODY,{"disambiguationData":[OSD([sQuery(id+"F5.wireOp",EDGE,"E13.bottom"),sQuery(id+"F5.wireOp",EDGE,"E13.top"),sQuery(id+"F5.wireOp",EDGE,"E13.left"),sQuery(id+"F5.wireOp",EDGE,"E13.right")])]});
            var Q23;
            Q23=makeQuery(id+"F7.opExtrude","SWEPT_BODY",BODY,{"disambiguationData":[OSD([sQuery(id+"F4.wireOp",EDGE,"E12.bottom"),sQuery(id+"F4.wireOp",EDGE,"E12.top"),sQuery(id+"F4.wireOp",EDGE,"E12.left"),sQuery(id+"F4.wireOp",EDGE,"E12.right")])]});
            var Q24;
            Q24=makeQuery(id+"F7.opExtrude","SWEPT_BODY",BODY,{"disambiguationData":[OSD([sQuery(id+"F2.wireOp",EDGE,"E8.bottom"),sQuery(id+"F2.wireOp",EDGE,"E8.top"),sQuery(id+"F2.wireOp",EDGE,"E8.left"),sQuery(id+"F2.wireOp",EDGE,"E8.right")])]});
            var Q25;
            Q25=makeQuery(id+"F7.opExtrude","SWEPT_BODY",BODY,{"disambiguationData":[OSD([sQuery(id+"F2.wireOp",EDGE,"E6.bottom"),sQuery(id+"F2.wireOp",EDGE,"E6.top"),sQuery(id+"F2.wireOp",EDGE,"E6.left"),sQuery(id+"F2.wireOp",EDGE,"E6.right")])]});
            var Q26;
            Q26=makeQuery(id+"F7.opExtrude","SWEPT_BODY",BODY,{"disambiguationData":[OSD([sQuery(id+"F3.wireOp",EDGE,"E9.bottom"),sQuery(id+"F3.wireOp",EDGE,"E9.top"),sQuery(id+"F3.wireOp",EDGE,"E9.left"),sQuery(id+"F3.wireOp",EDGE,"E9.right"),sQuery(id+"F3.wireOp",EDGE,"E10.bottom"),sQuery(id+"F3.wireOp",EDGE,"E10.top"),sQuery(id+"F3.wireOp",EDGE,"E10.right"),sQuery(id+"F3.wireOp",EDGE,"E11.bottom"),sQuery(id+"F3.wireOp",EDGE,"E11.top"),sQuery(id+"F3.wireOp",EDGE,"E11.right")])]});
            hole(context, id + "F43", {"style" : HoleStyle.SIMPLE, "endStyle" : HoleEndStyle.THROUGH, "holeDiameter" : 3 * mm, "locations" : qUnion([Q0, Q1, Q2, Q3, Q4, Q5, Q6, Q7, Q8, Q9, Q10, Q11, Q12, Q13, Q14, Q15, Q16, Q17, Q18, Q19]), "scope" : qUnion([Q20, Q21, Q22, Q23, Q24, Q25, Q26]), "isTappedThrough" : true});
        }
        {
            var Q0;
            Q0=makeQuery(id+"F17.opExtrude","SWEPT_FACE",FACE,{"disambiguationData":[OSD([sQuery(id+"F16.wireOp",EDGE,"E25.right")])]});
            var sketch = newSketch(context, id + "F44", { "sketchPlane" : qUnion([Q0])});
            skCircle(sketch, "E77", {"center": v(-370, 14.25) * mm, "radius": 1.5 * mm});
            skCircle(sketch, "E78", {"center": v(-319, 14.25) * mm, "radius": 1.5 * mm});
            skCircle(sketch, "E79", {"center": v(-268, 14.25) * mm, "radius": 1.5 * mm});
            skCircle(sketch, "E80", {"center": v(-217, 14.25) * mm, "radius": 1.5 * mm});
            skCircle(sketch, "E81", {"center": v(-166, 14.25) * mm, "radius": 1.5 * mm});
            skCircle(sketch, "E82", {"center": v(-115, 14.25) * mm, "radius": 1.5 * mm});
            skCircle(sketch, "E83", {"center": v(-64, 14.25) * mm, "radius": 1.5 * mm});
            skCircle(sketch, "E84", {"center": v(-13, 14.25) * mm, "radius": 1.5 * mm});
            skSolve(sketch);
        }
        {
            var Q0;
            Q0=sQuery(id+"F40.wireOp",VERTEX,"E42.center");
            var Q1;
            Q1=sQuery(id+"F40.wireOp",VERTEX,"E43.center");
            var Q2;
            Q2=sQuery(id+"F40.wireOp",VERTEX,"E44.center");
            var Q3;
            Q3=sQuery(id+"F40.wireOp",VERTEX,"E45.center");
            var Q4;
            Q4=sQuery(id+"F40.wireOp",VERTEX,"E46.center");
            var Q5;
            Q5=sQuery(id+"F40.wireOp",VERTEX,"E47.center");
            var Q6;
            Q6=sQuery(id+"F40.wireOp",VERTEX,"E48.center");
            var Q7;
            Q7=sQuery(id+"F40.wireOp",VERTEX,"E49.center");
            var Q8;
            Q8=sQuery(id+"F40.wireOp",VERTEX,"E50.center");
            var Q9;
            Q9=sQuery(id+"F40.wireOp",VERTEX,"E51.center");
            var Q10;
            Q10=sQuery(id+"F40.wireOp",VERTEX,"E52.center");
            var Q11;
            Q11=sQuery(id+"F40.wireOp",VERTEX,"E53.center");
            var Q12;
            Q12=sQuery(id+"F40.wireOp",VERTEX,"E54.center");
            var Q13;
            Q13=sQuery(id+"F40.wireOp",VERTEX,"E55.center");
            var Q14;
            Q14=sQuery(id+"F40.wireOp",VERTEX,"E56.center");
            var Q15;
            Q15=makeQuery(id+"F7.opExtrude","SWEPT_BODY",BODY,{"disambiguationData":[OSD([sQuery(id+"F1.wireOp",EDGE,"E3.bottom"),sQuery(id+"F1.wireOp",EDGE,"E3.top"),sQuery(id+"F1.wireOp",EDGE,"E3.left"),sQuery(id+"F1.wireOp",EDGE,"E3.right"),sQuery(id+"F1.wireOp",EDGE,"E4.bottom"),sQuery(id+"F1.wireOp",EDGE,"E4.top"),sQuery(id+"F1.wireOp",EDGE,"E4.right"),sQuery(id+"F1.wireOp",EDGE,"E5.bottom"),sQuery(id+"F1.wireOp",EDGE,"E5.top"),sQuery(id+"F1.wireOp",EDGE,"E5.right")])]});
            var Q16;
            Q16=makeQuery(id+"F7.opExtrude","SWEPT_BODY",BODY,{"disambiguationData":[OSD([sQuery(id+"F3.wireOp",EDGE,"E9.bottom"),sQuery(id+"F3.wireOp",EDGE,"E9.top"),sQuery(id+"F3.wireOp",EDGE,"E9.left"),sQuery(id+"F3.wireOp",EDGE,"E9.right"),sQuery(id+"F3.wireOp",EDGE,"E10.bottom"),sQuery(id+"F3.wireOp",EDGE,"E10.top"),sQuery(id+"F3.wireOp",EDGE,"E10.right"),sQuery(id+"F3.wireOp",EDGE,"E11.bottom"),sQuery(id+"F3.wireOp",EDGE,"E11.top"),sQuery(id+"F3.wireOp",EDGE,"E11.right")])]});
            var Q17;
            Q17=makeQuery(id+"F19.opExtrude","SWEPT_BODY",BODY,{"disambiguationData":[OSD([sQuery(id+"F18.wireOp",EDGE,"E27.bottom"),sQuery(id+"F18.wireOp",EDGE,"E27.top"),sQuery(id+"F18.wireOp",EDGE,"E27.left"),sQuery(id+"F18.wireOp",EDGE,"E27.right")])]});
            var Q18;
            Q18=makeQuery(id+"F7.opExtrude","SWEPT_BODY",BODY,{"disambiguationData":[OSD([sQuery(id+"F2.wireOp",EDGE,"E6.bottom"),sQuery(id+"F2.wireOp",EDGE,"E6.top"),sQuery(id+"F2.wireOp",EDGE,"E6.left"),sQuery(id+"F2.wireOp",EDGE,"E6.right")])]});
            var Q19;
            Q19=makeQuery(id+"F7.opExtrude","SWEPT_BODY",BODY,{"disambiguationData":[OSD([sQuery(id+"F2.wireOp",EDGE,"E8.bottom"),sQuery(id+"F2.wireOp",EDGE,"E8.top"),sQuery(id+"F2.wireOp",EDGE,"E8.left"),sQuery(id+"F2.wireOp",EDGE,"E8.right")])]});
            hole(context, id + "F45", {"style" : HoleStyle.SIMPLE, "endStyle" : HoleEndStyle.THROUGH, "holeDiameter" : 3 * mm, "locations" : qUnion([Q0, Q1, Q2, Q3, Q4, Q5, Q6, Q7, Q8, Q9, Q10, Q11, Q12, Q13, Q14]), "scope" : qUnion([Q15, Q16, Q17, Q18, Q19]), "isTappedThrough" : true});
        }
        {
            var Q0;
            Q0 = qSketchRegion(id + "F40", true);
            extrude(context, id + "F46", {"entities" : qUnion([Q0]), "operationType" : NewBodyOperationType.REMOVE, "oppositeDirection" : true, "depth" : 400 * mm});
        }
        {
            var Q0;
            Q0=makeQuery(id+"F7.opExtrude","SWEPT_EDGE",EDGE,{"disambiguationData":[OSD([sQuery(id+"F1.wireOp",EDGE,"E3.top"),sQuery(id+"F1.wireOp",EDGE,"E3.right")])]});
            fillet(context, id + "F47", {"entities" : qUnion([Q0]), "radius" : 4.2 * mm, "tangentPropagation" : true, "allowEdgeOverflow" : false});
        }
    });
